annotation { "Feature Type Name" : "Feature", "Feature Type Description" : "" }
export const myFeature = defineFeature(function(context is Context, id is Id, definition is map)
    precondition{}
    {
        {
            var Q0;
            Q0=qCreatedBy(makeId("Front.planeOp"),FACE);
            var sketch = newSketch(context, id + "F0", { "sketchPlane" : qUnion([Q0])});
            skLineSegment(sketch, "E0.bottom", {"start": v(6.46, -3.5) * mm, "end": v(-6.88, -3.5) * mm});
            skLineSegment(sketch, "E0.top", {"start": v(6.88, 3.5) * mm, "end": v(-6.46, 3.5) * mm});
            skPoint(sketch, "E0.middle", {"position": v(0, 0) * mm});
            skArc(sketch, "E1", {"start": v(6.46, -3.5) * mm, "mid": v(10, -0.2) * mm, "end": v(6.88, 3.5) * mm});
            skArc(sketch, "E2", {"start": v(-6.46, 3.5) * mm, "mid": v(-9.96, 0.2) * mm, "end": v(-6.88, -3.5) * mm});
            skLineSegment(sketch, "E3.bottom", {"start": v(6.94, -5.5) * mm, "end": v(-6.4, -5.5) * mm});
            skLineSegment(sketch, "E3.top", {"start": v(6.4, 5.5) * mm, "end": v(-6.94, 5.5) * mm});
            skArc(sketch, "E4", {"start": v(6.94, -5.5) * mm, "mid": v(11.9, 0.25) * mm, "end": v(6.4, 5.5) * mm});
            skArc(sketch, "E5", {"start": v(-6.94, 5.5) * mm, "mid": v(-12.44, -0.28) * mm, "end": v(-6.4, -5.5) * mm});
            skPoint(sketch, "E6", {"position": v(-9.96, -0.01) * mm});
            skSolve(sketch);
        }
        {
            var Q0;
            Q0=makeQuery(id+"F0.imprint","IMPRINT",FACE,{"disambiguationData":[TD([[makeQuery(id+"F0.imprint","IMPRINT",EDGE,{"derivedFrom":sQuery(id+"F0.wireOp",EDGE,"E0.bottom")}),1.0]])]});
            extrude(context, id + "F1", {"entities" : qUnion([Q0]), "depth" : 55.88 * mm});
        }
        {
            var Q0;
            Q0=makeQuery(id+"F1.opExtrude","CAP_FACE",FACE,{"disambiguationData":[OSD([sQuery(id+"F0.wireOp",EDGE,"E0.bottom"),sQuery(id+"F0.wireOp",EDGE,"E0.top"),sQuery(id+"F0.wireOp",EDGE,"E1"),sQuery(id+"F0.wireOp",EDGE,"E2"),sQuery(id+"F0.wireOp",EDGE,"E3.bottom"),sQuery(id+"F0.wireOp",EDGE,"E3.top"),sQuery(id+"F0.wireOp",EDGE,"E4"),sQuery(id+"F0.wireOp",EDGE,"E5")])],"isStart":false});
            var sketch = newSketch(context, id + "F2", { "sketchPlane" : qUnion([Q0])});
            skLineSegment(sketch, "E7.bottom", {"start": v(-17.6, 8.08) * mm, "end": v(19.99, 8.08) * mm});
            skLineSegment(sketch, "E7.top", {"start": v(-17.6, 2.54) * mm, "end": v(19.99, 2.54) * mm});
            skLineSegment(sketch, "E7.left", {"start": v(-17.6, 8.08) * mm, "end": v(-17.6, 2.54) * mm});
            skLineSegment(sketch, "E7.right", {"start": v(19.99, 8.08) * mm, "end": v(19.99, 2.54) * mm});
            skSolve(sketch);
        }
        {
            var Q0;
            Q0=makeQuery(id+"F2.imprint","IMPRINT",FACE,{"disambiguationData":[TD([[makeQuery(id+"F2.imprint","IMPRINT",EDGE,{"derivedFrom":sQuery(id+"F2.wireOp",EDGE,"E7.bottom")}),-1.0]])]});
            var Q1;
            {var subQ6=makeQuery(id+"F1.opExtrude","CAP_EDGE",EDGE,{"disambiguationData":[OSD([sQuery(id+"F0.wireOp",EDGE,"E0.top")])],"isStart":false});Q1=makeQuery(id+"F2.imprint","IMPRINT",FACE,{"disambiguationData":[TD([[makeQuery(id+"F2.imprint","IMPRINT",EDGE,{"derivedFrom":subQ6}),-1.0]])]});}
            extrude(context, id + "F3", {"entities" : qUnion([Q0, Q1]), "operationType" : NewBodyOperationType.REMOVE, "oppositeDirection" : true, "depth" : 55.88 * mm});
        }
        {
            var Q0;
            Q0=makeQuery(id+"F1.opExtrude","SWEPT_FACE",FACE,{"disambiguationData":[OSD([sQuery(id+"F0.wireOp",EDGE,"E3.bottom")])]});
            var sketch = newSketch(context, id + "F4", { "sketchPlane" : qUnion([Q0])});
            skText(sketch, "E8", { "text": "Jay Chen", "fontName": "AllertaStencil-Regular.ttf"});
            const initialGuessF4  = {"E8": [-0.0036, 0.05169, 0, -1, 0.00762]};
            skSetInitialGuess(sketch, initialGuessF4);
            skSolve(sketch);
        }
        {
            var Q0;
            Q0 = qSketchRegion(id + "F4", true);
            extrude(context, id + "F5", {"entities" : qUnion([Q0]), "operationType" : NewBodyOperationType.REMOVE, "oppositeDirection" : true, "depth" : 25.4 * mm});
        }
    });